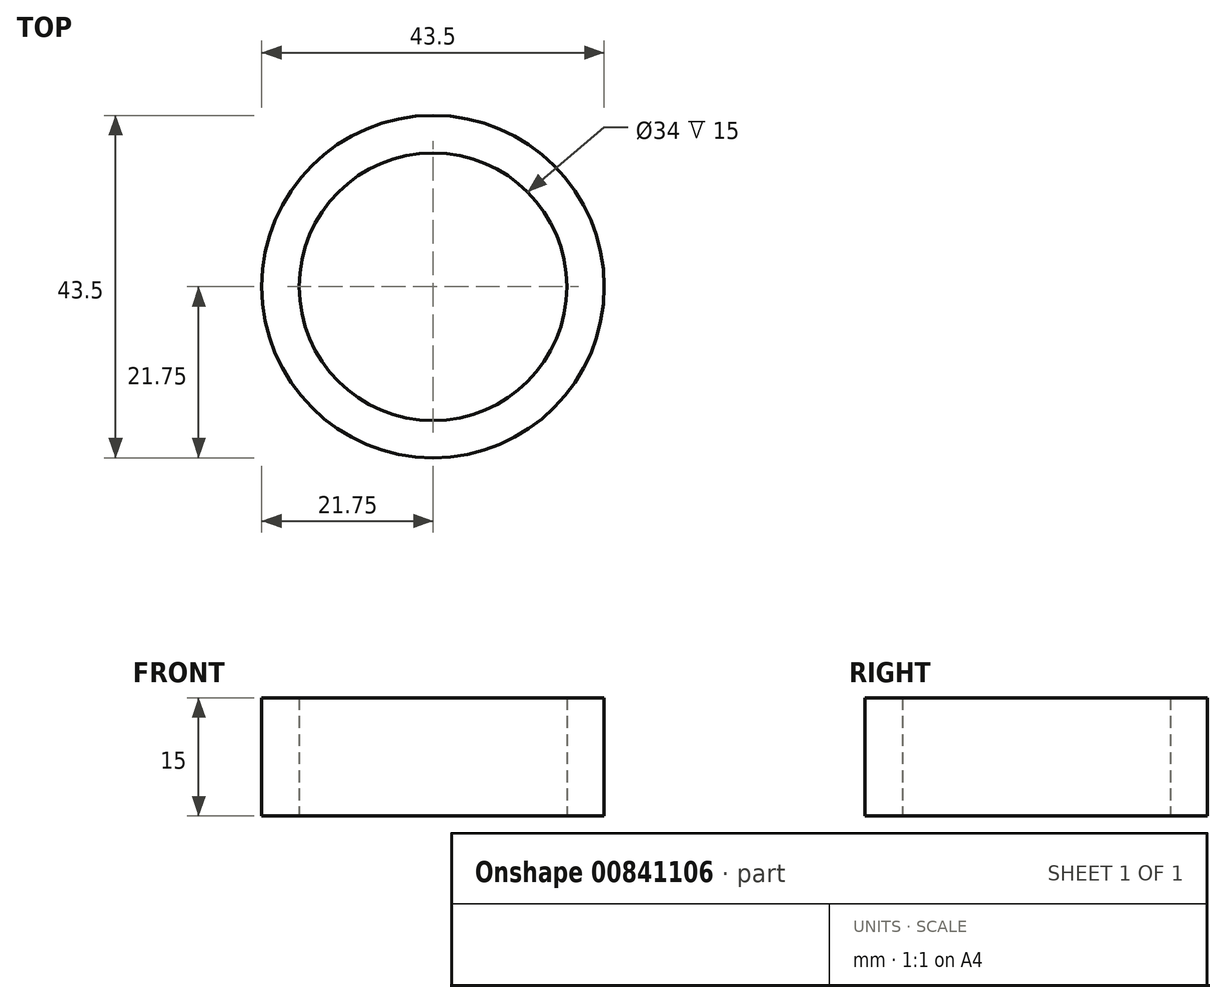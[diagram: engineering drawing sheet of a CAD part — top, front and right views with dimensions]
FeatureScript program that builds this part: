
annotation { "Feature Type Name" : "Feature", "Feature Type Description" : "" }
export const myFeature = defineFeature(function(context is Context, id is Id, definition is map)
    precondition{}
    {
        {
            var Q0;
            Q0=qCreatedBy(makeId("Top.planeOp"),FACE);
            var sketch = newSketch(context, id + "F0", { "sketchPlane" : qUnion([Q0])});
            skCircle(sketch, "E0", {"center": v(0, 0) * mm, "radius": 17 * mm});
            skCircle(sketch, "E1", {"center": v(0, 0) * mm, "radius": 21.75 * mm});
            skSolve(sketch);
        }
        {
            var Q0;
            Q0=makeQuery(id+"F0.imprint","IMPRINT",FACE,{"disambiguationData":[TD([[makeQuery(id+"F0.imprint","IMPRINT",EDGE,{"derivedFrom":sQuery(id+"F0.wireOp",EDGE,"E0")}),-1.0]])]});
            extrude(context, id + "F1", {"entities" : qUnion([Q0]), "depth" : 15 * mm, "offsetDistance" : 25 * mm});
        }
    });
